# Revit family: WC-Close Coupled-Caroma Caravelle Suite with Armrest
name_source: partatom
category: Plumbing Fixtures
revit_build: Autodesk Revit 2015 (Build: 20140606_1530(x64)
units: mm (PartAtom-declared; Revit-internal decimal feet)

## types (1)
- Standard
    Assembly Code = D2010110
    CW Connection = No
    CWFU = 0
    Description = The Caravelle Easy Height, with its sophisticated design, offers an elevated pan for those with restricted movement. Includes  stainless steel armrests.
    HW Connection = No
    Hardware = Metal-Stainless Steel-Brushed
    Height_ANZRS = 850 mm  [stored 2.78871 ft]
    Length_ANZRS = 660 mm
    Manufacturer = GWA Bathrooms & Kitchens
    Material_ANZRS = Porcelain-White-Caroma
    Model = 989250ARW
    ModifiedIssue_ANZRS = 20160630.54 $
    Type Comments = Caravelle EH Close Coupled Suite w Armrest
    URL = http://specify.caroma.com.au
    Vent Connection = No
    WELSRating_ANZRS = WELS 4 Star rated, 4.5/3L
    WFU = 0
    Waste Connection = No
    WasteOutlet_ANZRS = 0
    Width_ANZRS = 365 mm  [stored 1.19751 ft]

note: [stored X ft] marks values corroborated as IEEE doubles in the binary element streams (Revit-internal decimal feet)

## geometry (parser evidence)
native form markers: Blend x2, Sweep x3
no freeform markers — native parametric forms only
